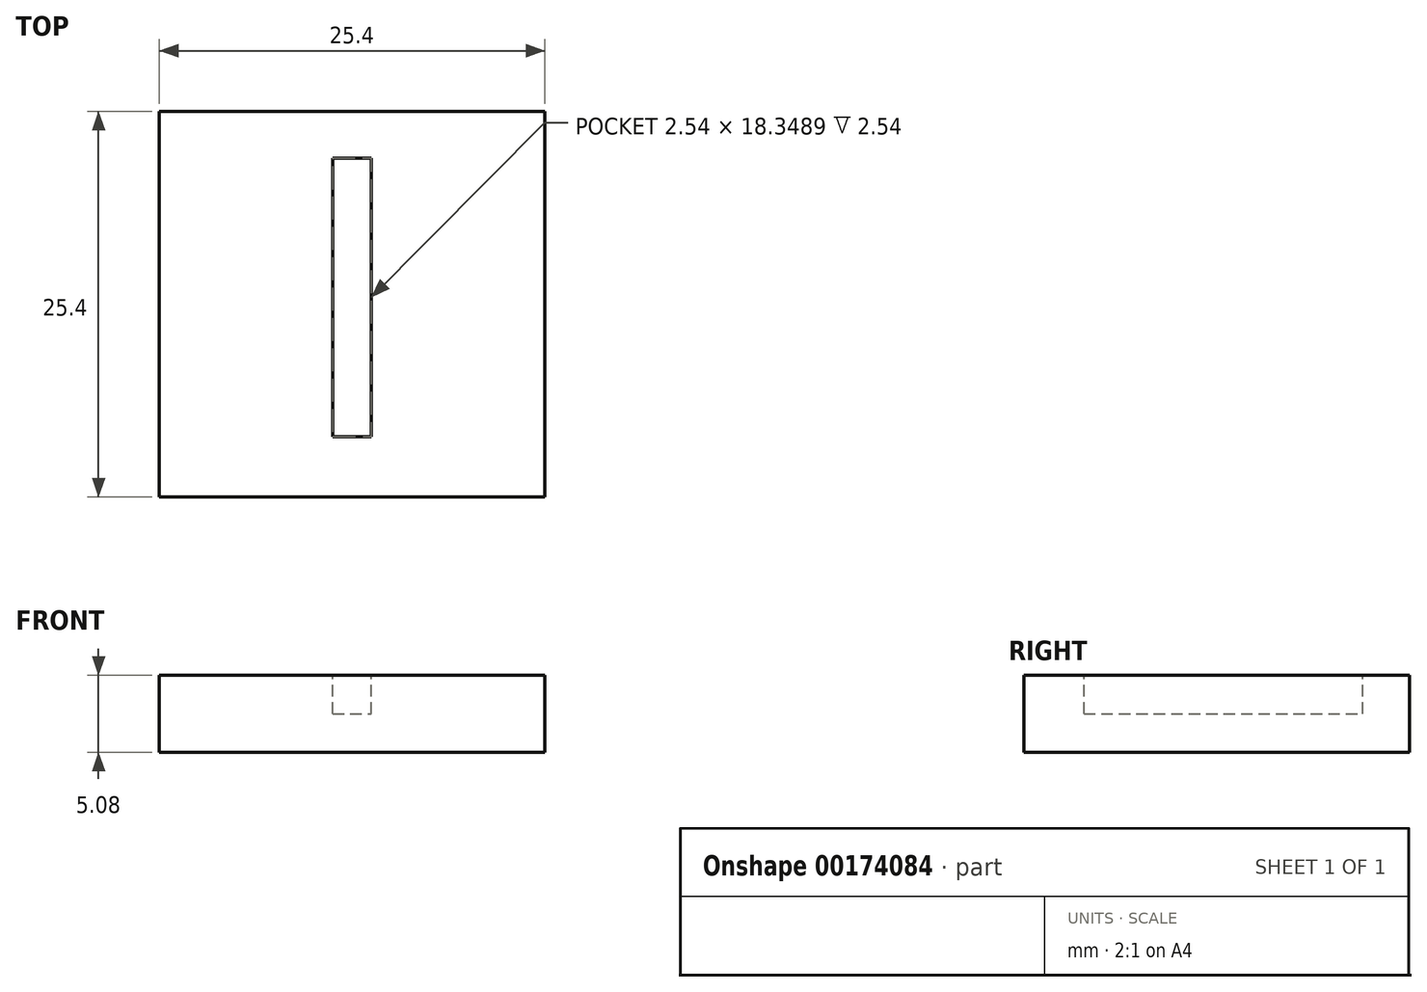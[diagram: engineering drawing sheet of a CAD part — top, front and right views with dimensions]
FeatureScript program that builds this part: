
annotation { "Feature Type Name" : "Feature", "Feature Type Description" : "" }
export const myFeature = defineFeature(function(context is Context, id is Id, definition is map)
    precondition{}
    {
        {
            var Q0;
            Q0=qCreatedBy(makeId("Top.planeOp"),FACE);
            var sketch = newSketch(context, id + "F0", { "sketchPlane" : qUnion([Q0])});
            skLineSegment(sketch, "E0.bottom", {"start": v(12.7, -12.7) * mm, "end": v(-12.7, -12.7) * mm});
            skLineSegment(sketch, "E0.top", {"start": v(12.7, 12.7) * mm, "end": v(-12.7, 12.7) * mm});
            skLineSegment(sketch, "E0.left", {"start": v(12.7, -12.7) * mm, "end": v(12.7, 12.7) * mm});
            skLineSegment(sketch, "E0.right", {"start": v(-12.7, -12.7) * mm, "end": v(-12.7, 12.7) * mm});
            skPoint(sketch, "E0.middle", {"position": v(0, 0) * mm});
            skSolve(sketch);
        }
        {
            var Q0;
            Q0 = qSketchRegion(id + "F0", true);
            extrude(context, id + "F1", {"entities" : qUnion([Q0]), "depth" : 5.08 * mm});
        }
        {
            var Q0;
            Q0=makeQuery(id+"F1.opExtrude","CAP_FACE",FACE,{"disambiguationData":[OSD([sQuery(id+"F0.wireOp",EDGE,"E0.bottom"),sQuery(id+"F0.wireOp",EDGE,"E0.top"),sQuery(id+"F0.wireOp",EDGE,"E0.left"),sQuery(id+"F0.wireOp",EDGE,"E0.right")])],"isStart":false});
            var sketch = newSketch(context, id + "F2", { "sketchPlane" : qUnion([Q0])});
            skLineSegment(sketch, "E1.left", {"start": v(1.27, -8.73) * mm, "end": v(1.27, 9.62) * mm});
            skLineSegment(sketch, "E1.right", {"start": v(-1.27, -8.73) * mm, "end": v(-1.27, 9.62) * mm});
            skPoint(sketch, "E1.middle", {"position": v(0, 0) * mm});
            skLineSegment(sketch, "E2", {"start": v(-1.27, 9.62) * mm, "end": v(1.27, 9.62) * mm});
            skLineSegment(sketch, "E3", {"start": v(-1.27, -8.73) * mm, "end": v(1.27, -8.73) * mm});
            skPoint(sketch, "E1.top.end.orphan", {"position": v(-1.27, 12.7) * mm});
            skPoint(sketch, "E1.top.start.orphan", {"position": v(1.27, 12.7) * mm});
            skPoint(sketch, "E4.orphan", {"position": v(-1.27, -12.7) * mm});
            skPoint(sketch, "E5.orphan", {"position": v(1.27, -12.7) * mm});
            skSolve(sketch);
        }
        {
            var Q0;
            Q0 = qSketchRegion(id + "F2", true);
            extrude(context, id + "F3", {"entities" : qUnion([Q0]), "operationType" : NewBodyOperationType.REMOVE, "oppositeDirection" : true, "depth" : 2.54 * mm});
        }
    });
